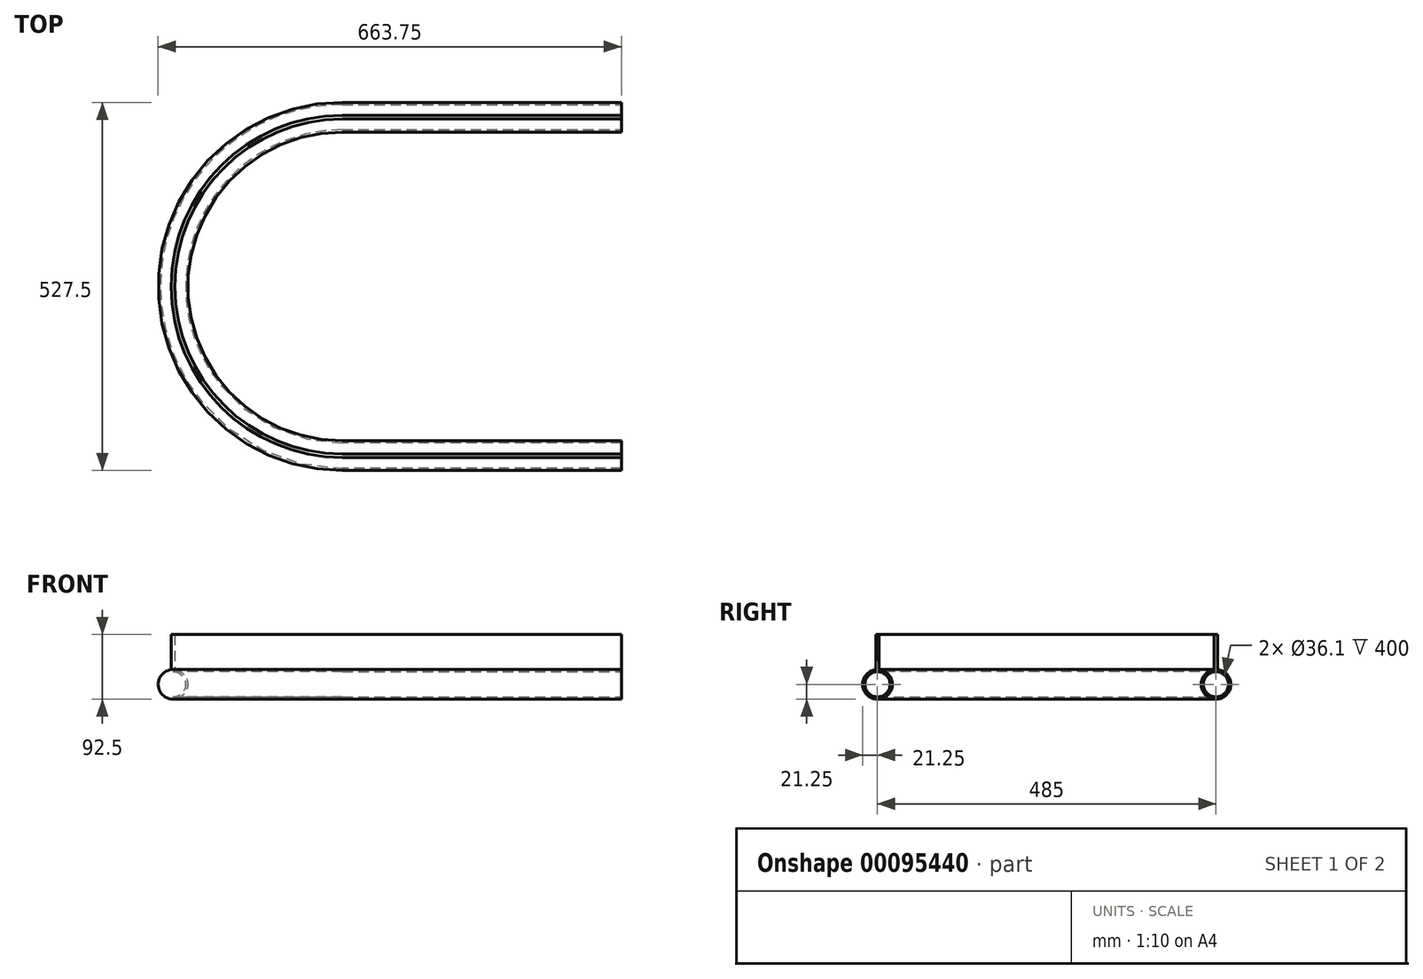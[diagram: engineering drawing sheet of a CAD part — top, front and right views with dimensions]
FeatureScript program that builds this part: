
annotation { "Feature Type Name" : "Feature", "Feature Type Description" : "" }
export const myFeature = defineFeature(function(context is Context, id is Id, definition is map)
    precondition{}
    {
        {
            var Q0;
            Q0=qCreatedBy(makeId("Top.planeOp"),FACE);
            var sketch = newSketch(context, id + "F0", { "sketchPlane" : qUnion([Q0])});
            skLineSegment(sketch, "E0", {"start": v(-400, 242.5) * mm, "end": v(0, 242.5) * mm});
            skArc(sketch, "E1", {"start": v(-400, 242.5) * mm, "mid": v(-642.5, 0) * mm, "end": v(-400, -242.5) * mm});
            skLineSegment(sketch, "E2", {"start": v(-400, -242.5) * mm, "end": v(0, -242.5) * mm});
            skSolve(sketch);
        }
        {
            var Q0;
            Q0=qCreatedBy(makeId("Right.planeOp"),FACE);
            var sketch = newSketch(context, id + "F1", { "sketchPlane" : qUnion([Q0])});
            skArc(sketch, "E3", {"start": v(-245, -0.15) * mm, "mid": v(-242.5, -42.5) * mm, "end": v(-240, -0.15) * mm});
            skLineSegment(sketch, "E4.0", {"start": v(-242.5, 0) * mm, "end": v(0, 0) * mm, "construction": true});
            skLineSegment(sketch, "E5.bottom", {"start": v(-245, 50) * mm, "end": v(-240, 50) * mm});
            skLineSegment(sketch, "E5.left", {"start": v(-245, 50) * mm, "end": v(-245, -0.15) * mm});
            skLineSegment(sketch, "E5.right", {"start": v(-240, 50) * mm, "end": v(-240, -0.15) * mm});
            skLineSegment(sketch, "E6", {"start": v(-242.5, 50) * mm, "end": v(-242.5, -1.76) * mm, "construction": true});
            skLineSegment(sketch, "E7", {"start": v(-242.5, -21.25) * mm, "end": v(-242.5, 90.65) * mm, "construction": true});
            skCircle(sketch, "E8", {"center": v(-242.5, -21.25) * mm, "radius": 18.05 * mm});
            skSolve(sketch);
        }
        {
            var Q0;
            Q0=makeQuery(id+"F1.imprint","IMPRINT",FACE,{"disambiguationData":[TD([[makeQuery(id+"F1.imprint","IMPRINT",EDGE,{"derivedFrom":sQuery(id+"F1.wireOp",EDGE,"E3")}),1.0]])]});
            var Q1;
            Q1=sQuery(id+"F0.wireOp",EDGE,"E2");
            var Q2;
            Q2=sQuery(id+"F0.wireOp",EDGE,"E1");
            var Q3;
            Q3=sQuery(id+"F0.wireOp",EDGE,"E0");
            sweep(context, id + "F2", {"profiles" : qUnion([Q0]), "path" : qUnion([Q1, Q2, Q3])});
        }
    });
